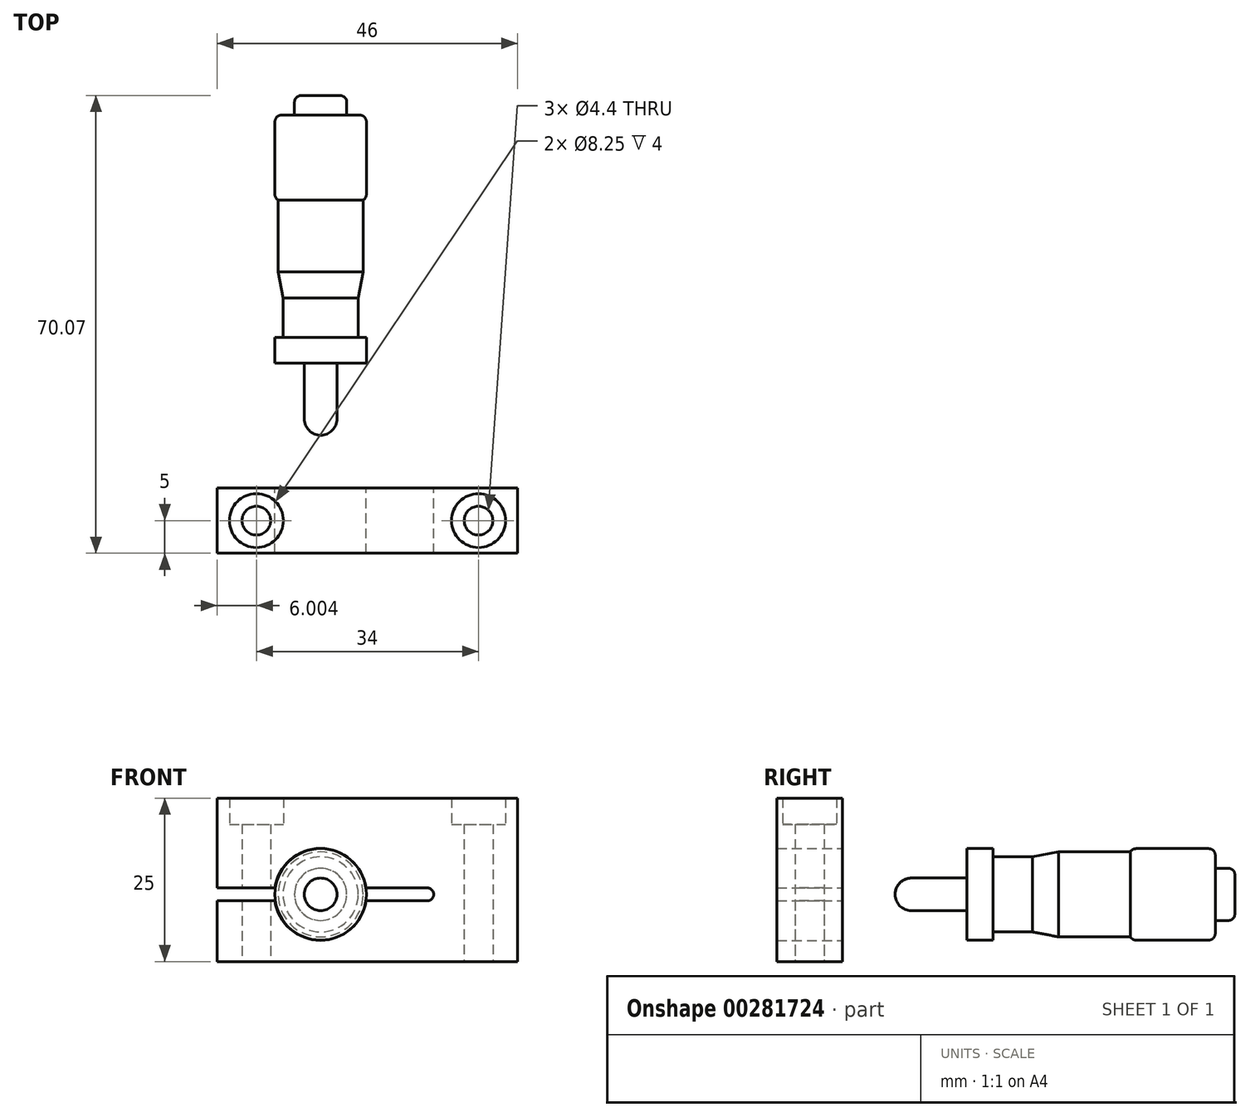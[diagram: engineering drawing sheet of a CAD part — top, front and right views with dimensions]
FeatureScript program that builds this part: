
annotation { "Feature Type Name" : "Feature", "Feature Type Description" : "" }
export const myFeature = defineFeature(function(context is Context, id is Id, definition is map)
    precondition{}
    {
        {
            var Q0;
            Q0=qCreatedBy(makeId("Right.planeOp"),FACE);
            var sketch = newSketch(context, id + "F0", { "sketchPlane" : qUnion([Q0])});
            skLineSegment(sketch, "E0", {"start": v(4.07, 5.75) * mm, "end": v(8.07, 6.5) * mm});
            skLineSegment(sketch, "E1", {"start": v(8.07, 6.5) * mm, "end": v(19.07, 6.5) * mm});
            skLineSegment(sketch, "E2", {"start": v(19.07, 6.5) * mm, "end": v(19.07, 7) * mm});
            skLineSegment(sketch, "E3", {"start": v(19.07, 7) * mm, "end": v(32.07, 7) * mm});
            skLineSegment(sketch, "E4", {"start": v(32.07, 7) * mm, "end": v(32.07, 4) * mm});
            skLineSegment(sketch, "E5", {"start": v(32.07, 4) * mm, "end": v(35.07, 4) * mm});
            skLineSegment(sketch, "E6", {"start": v(35.07, 4) * mm, "end": v(35.07, 0) * mm});
            skLineSegment(sketch, "E7", {"start": v(4.07, 5.75) * mm, "end": v(-1.93, 5.75) * mm});
            skLineSegment(sketch, "E8", {"start": v(-1.93, 5.75) * mm, "end": v(-1.93, 7) * mm});
            skLineSegment(sketch, "E9", {"start": v(-1.93, 7) * mm, "end": v(-5.93, 7) * mm});
            skLineSegment(sketch, "E10", {"start": v(-5.93, 7) * mm, "end": v(-5.93, 2.5) * mm});
            skLineSegment(sketch, "E11", {"start": v(-5.93, 2.5) * mm, "end": v(-16.93, 2.5) * mm});
            skLineSegment(sketch, "E12", {"start": v(-16.93, 2.5) * mm, "end": v(-16.93, 0) * mm});
            skLineSegment(sketch, "E13", {"start": v(-16.93, 0) * mm, "end": v(35.07, 0) * mm});
            skSolve(sketch);
        }
        {
            var Q0;
            Q0 = qSketchRegion(id + "F0", true);
            var Q1;
            Q1=sQuery(id+"F0.wireOp",EDGE,"E13");
            revolve(context, id + "F1", {"surfaceOperationType" : NewSurfaceOperationType.NEW, "entities" : qUnion([Q0]), "axis" : qUnion([Q1]), "revolveType" : RevolveType.FULL});
        }
        {
            var Q0;
            Q0=makeQuery(id+"F1.opRevolve","SWEPT_EDGE",EDGE,{"disambiguationData":[OSD([sQuery(id+"F0.wireOp",EDGE,"E5"),sQuery(id+"F0.wireOp",EDGE,"E6")])]});
            var Q1;
            Q1=makeQuery(id+"F1.opRevolve","SWEPT_EDGE",EDGE,{"disambiguationData":[OSD([sQuery(id+"F0.wireOp",EDGE,"E3"),sQuery(id+"F0.wireOp",EDGE,"E4")])]});
            var Q2;
            Q2=makeQuery(id+"F1.opRevolve","SWEPT_EDGE",EDGE,{"disambiguationData":[OSD([sQuery(id+"F0.wireOp",EDGE,"E2"),sQuery(id+"F0.wireOp",EDGE,"E3")])]});
            fillet(context, id + "F2", {"entities" : qUnion([Q0, Q1, Q2]), "radius" : 1 * mm, "tangentPropagation" : true, "allowEdgeOverflow" : false});
        }
        {
            var Q0;
            Q0=makeQuery(id+"F1.opRevolve","SWEPT_EDGE",EDGE,{"disambiguationData":[OSD([sQuery(id+"F0.wireOp",EDGE,"E11"),sQuery(id+"F0.wireOp",EDGE,"E12")])]});
            fillet(context, id + "F3", {"entities" : qUnion([Q0]), "radius" : 2.5 * mm, "tangentPropagation" : true, "allowEdgeOverflow" : false});
        }
        {
            var Q0;
            Q0=qCreatedBy(makeId("Front.planeOp"),FACE);
            cPlane(context, id + "F4", {"entities" : qUnion([Q0]), "cplaneType" : CPlaneType.OFFSET, "offset" : 25 * mm, "width" : 150 * mm, "height" : 150 * mm});
        }
        {
            var Q0;
            Q0=qCreatedBy(id+"F4.planeOp",FACE);
            var sketch = newSketch(context, id + "F5", { "sketchPlane" : qUnion([Q0])});
            skLineSegment(sketch, "E14.bottom", {"start": v(30.16, -10.28) * mm, "end": v(-15.84, -10.28) * mm});
            skLineSegment(sketch, "E14.top", {"start": v(30.16, 14.72) * mm, "end": v(-15.84, 14.72) * mm});
            skLineSegment(sketch, "E14.left", {"start": v(30.16, -10.28) * mm, "end": v(30.16, 14.72) * mm});
            skLineSegment(sketch, "E14.right", {"start": v(-15.84, -10.28) * mm, "end": v(-15.84, -1) * mm});
            skCircle(sketch, "E15", {"center": v(-0.04, 0) * mm, "radius": 7.04 * mm});
            skArc(sketch, "E16.0.startCap", {"start": v(16.3, 1) * mm, "mid": v(17.3, 0) * mm, "end": v(16.3, -1) * mm});
            skLineSegment(sketch, "E16.0.left", {"start": v(16.3, -1) * mm, "end": v(-15.84, -1) * mm});
            skLineSegment(sketch, "E16.0.right", {"start": v(16.3, 1) * mm, "end": v(-15.84, 1) * mm});
            skLineSegment(sketch, "E17.trimOffspring", {"start": v(-15.84, 1) * mm, "end": v(-15.84, 14.72) * mm});
            skSolve(sketch);
        }
        {
            var Q0;
            Q0=makeQuery(id+"F5.imprint","IMPRINT",FACE,{"disambiguationData":[TD([[makeQuery(id+"F5.imprint","IMPRINT",EDGE,{"derivedFrom":sQuery(id+"F5.wireOp",EDGE,"E14.bottom")}),-1.0]])]});
            extrude(context, id + "F6", {"entities" : qUnion([Q0]), "depth" : 10 * mm, "offsetDistance" : 25 * mm});
        }
        {
            var Q0;
            Q0=makeQuery(id+"F6.opExtrude","SWEPT_FACE",FACE,{"disambiguationData":[OSD([sQuery(id+"F5.wireOp",EDGE,"E14.top")])]});
            var sketch = newSketch(context, id + "F7", { "sketchPlane" : qUnion([Q0])});
            skLineSegment(sketch, "E18", {"start": v(-15.84, -30) * mm, "end": v(30.16, -30) * mm, "construction": true});
            skPoint(sketch, "E19", {"position": v(24.16, -30) * mm});
            skPoint(sketch, "E20", {"position": v(-9.84, -30) * mm});
            skSolve(sketch);
        }
        {
            var Q0;
            Q0=sQuery(id+"F7.wireOp",VERTEX,"E19");
            var Q1;
            Q1=sQuery(id+"F7.wireOp",VERTEX,"E20");
            var Q2;
            Q2=makeQuery(id+"F6.opExtrude","SWEPT_BODY",BODY,{"disambiguationData":[OSD([sQuery(id+"F5.wireOp",EDGE,"E14.bottom"),sQuery(id+"F5.wireOp",EDGE,"E14.top"),sQuery(id+"F5.wireOp",EDGE,"E14.left"),sQuery(id+"F5.wireOp",EDGE,"E14.right"),sQuery(id+"F5.wireOp",EDGE,"E15"),sQuery(id+"F5.wireOp",EDGE,"E16.0.startCap"),sQuery(id+"F5.wireOp",EDGE,"E16.0.left"),sQuery(id+"F5.wireOp",EDGE,"E16.0.right"),sQuery(id+"F5.wireOp",EDGE,"E17.trimOffspring")])]});
            hole(context, id + "F8", {"style" : HoleStyle.C_BORE, "endStyle" : HoleEndStyle.THROUGH, "standardTappedOrClearance" : lookupTablePath({ "fit" : "Normal", "standard" : "ISO", "size" : "M4", "type" : "Clearance" }), "standardBlindInLast" : lookupTablePath({ "fit" : "Standard", "standard" : "ISO", "size" : "M4", "type" : "Clearance" }), "holeDiameter" : 4.4 * mm, "cBoreDiameter" : 8.25 * mm, "cBoreDepth" : 4 * mm, "majorDiameter" : 4 * mm, "isTappedThrough" : true, "tappedDepth" : 12 * mm, "tapClearance" : 3, "locations" : qUnion([Q0, Q1]), "scope" : qUnion([Q2]), "startStyle" : HoleStartStyle.PART});
        }
    });
